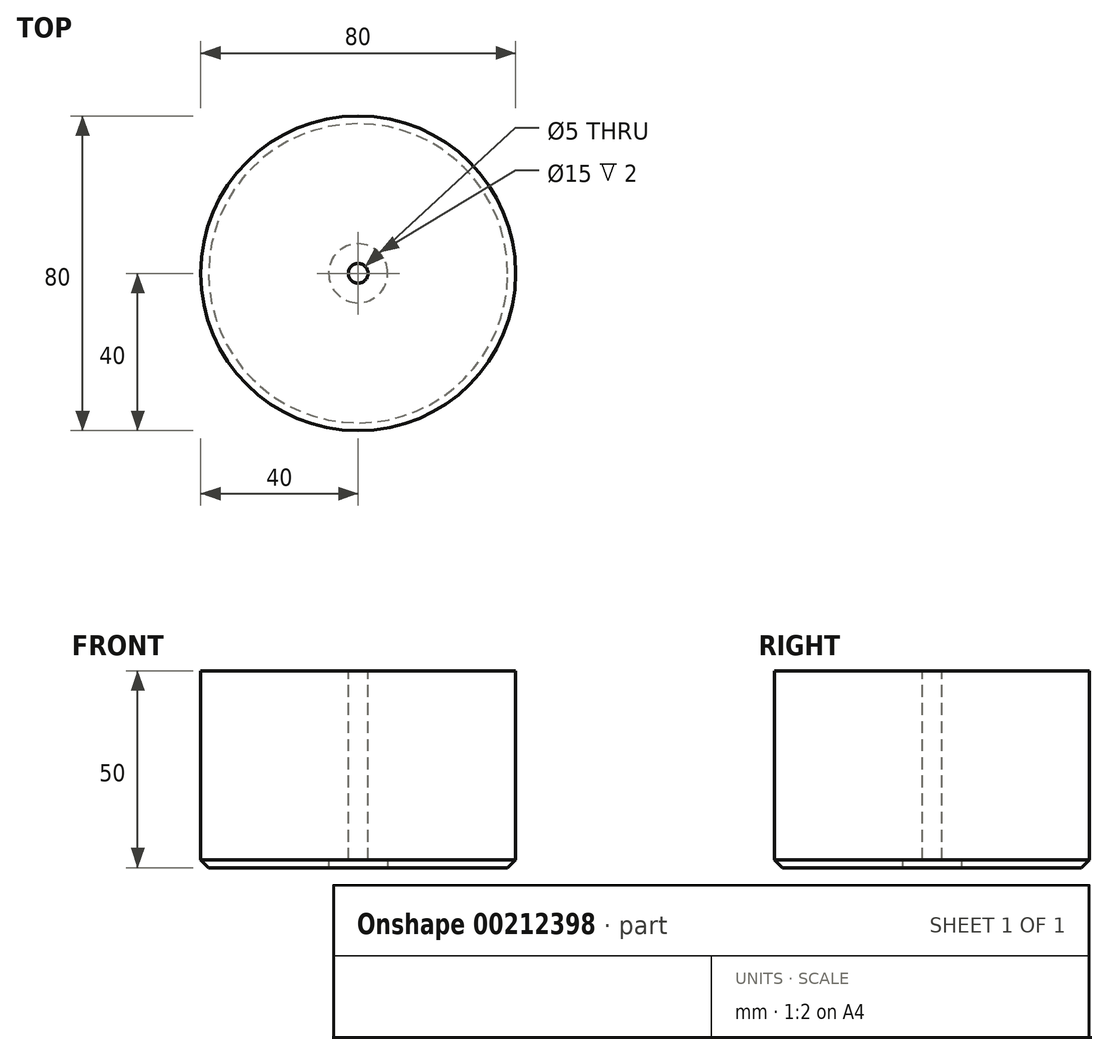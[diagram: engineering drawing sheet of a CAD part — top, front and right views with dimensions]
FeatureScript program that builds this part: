
annotation { "Feature Type Name" : "Feature", "Feature Type Description" : "" }
export const myFeature = defineFeature(function(context is Context, id is Id, definition is map)
    precondition{}
    {
        {
            var Q0;
            Q0=qCreatedBy(makeId("Top.planeOp"),FACE);
            var sketch = newSketch(context, id + "F0", { "sketchPlane" : qUnion([Q0])});
            skCircle(sketch, "E0", {"center": v(0, 0) * mm, "radius": 40 * mm});
            skSolve(sketch);
        }
        {
            var Q0;
            Q0=makeQuery(id+"F0.imprint","IMPRINT",FACE,{"disambiguationData":[TD([[makeQuery(id+"F0.imprint","IMPRINT",EDGE,{"derivedFrom":sQuery(id+"F0.wireOp",EDGE,"E0")}),1.0]])]});
            extrude(context, id + "F1", {"entities" : qUnion([Q0]), "depth" : 50 * mm});
        }
        {
            var Q0;
            Q0=makeQuery(id+"F1.opExtrude","CAP_FACE",FACE,{"disambiguationData":[OSD([sQuery(id+"F0.wireOp",EDGE,"E0")])],"isStart":false});
            var sketch = newSketch(context, id + "F2", { "sketchPlane" : qUnion([Q0])});
            skCircle(sketch, "E1", {"center": v(0, 0) * mm, "radius": 2.5 * mm});
            skSolve(sketch);
        }
        {
            var Q0;
            Q0=makeQuery(id+"F2.imprint","IMPRINT",FACE,{"disambiguationData":[TD([[makeQuery(id+"F2.imprint","IMPRINT",EDGE,{"derivedFrom":sQuery(id+"F2.wireOp",EDGE,"E1")}),1.0]])]});
            var Q1;
            Q1=sQuery(id+"F2.wireOp",EDGE,"E1");
            extrude(context, id + "F3", {"entities" : qUnion([Q0]), "operationType" : NewBodyOperationType.REMOVE, "surfaceEntities" : qUnion([Q1]), "oppositeDirection" : true, "depth" : 50 * mm});
        }
        {
            var Q0;
            Q0=makeQuery(id+"F1.opExtrude","CAP_FACE",FACE,{"disambiguationData":[OSD([sQuery(id+"F0.wireOp",EDGE,"E0")])],"isStart":true});
            var sketch = newSketch(context, id + "F4", { "sketchPlane" : qUnion([Q0])});
            skCircle(sketch, "E2", {"center": v(0, 0) * mm, "radius": 7.5 * mm});
            skSolve(sketch);
        }
        {
            var Q0;
            Q0=makeQuery(id+"F4.imprint","IMPRINT",FACE,{"disambiguationData":[TD([[makeQuery(id+"F4.imprint","IMPRINT",EDGE,{"derivedFrom":sQuery(id+"F4.wireOp",EDGE,"E2")}),1.0]])]});
            extrude(context, id + "F5", {"entities" : qUnion([Q0]), "operationType" : NewBodyOperationType.REMOVE, "oppositeDirection" : true, "depth" : 2 * mm});
        }
        {
            var Q0;
            Q0=makeQuery(id+"F1.opExtrude","CAP_EDGE",EDGE,{"disambiguationData":[OSD([sQuery(id+"F0.wireOp",EDGE,"E0")])],"isStart":true});
            chamfer(context, id + "F6", {"entities" : qUnion([Q0]), "width" : 2 * mm, "tangentPropagation" : true});
        }
    });
